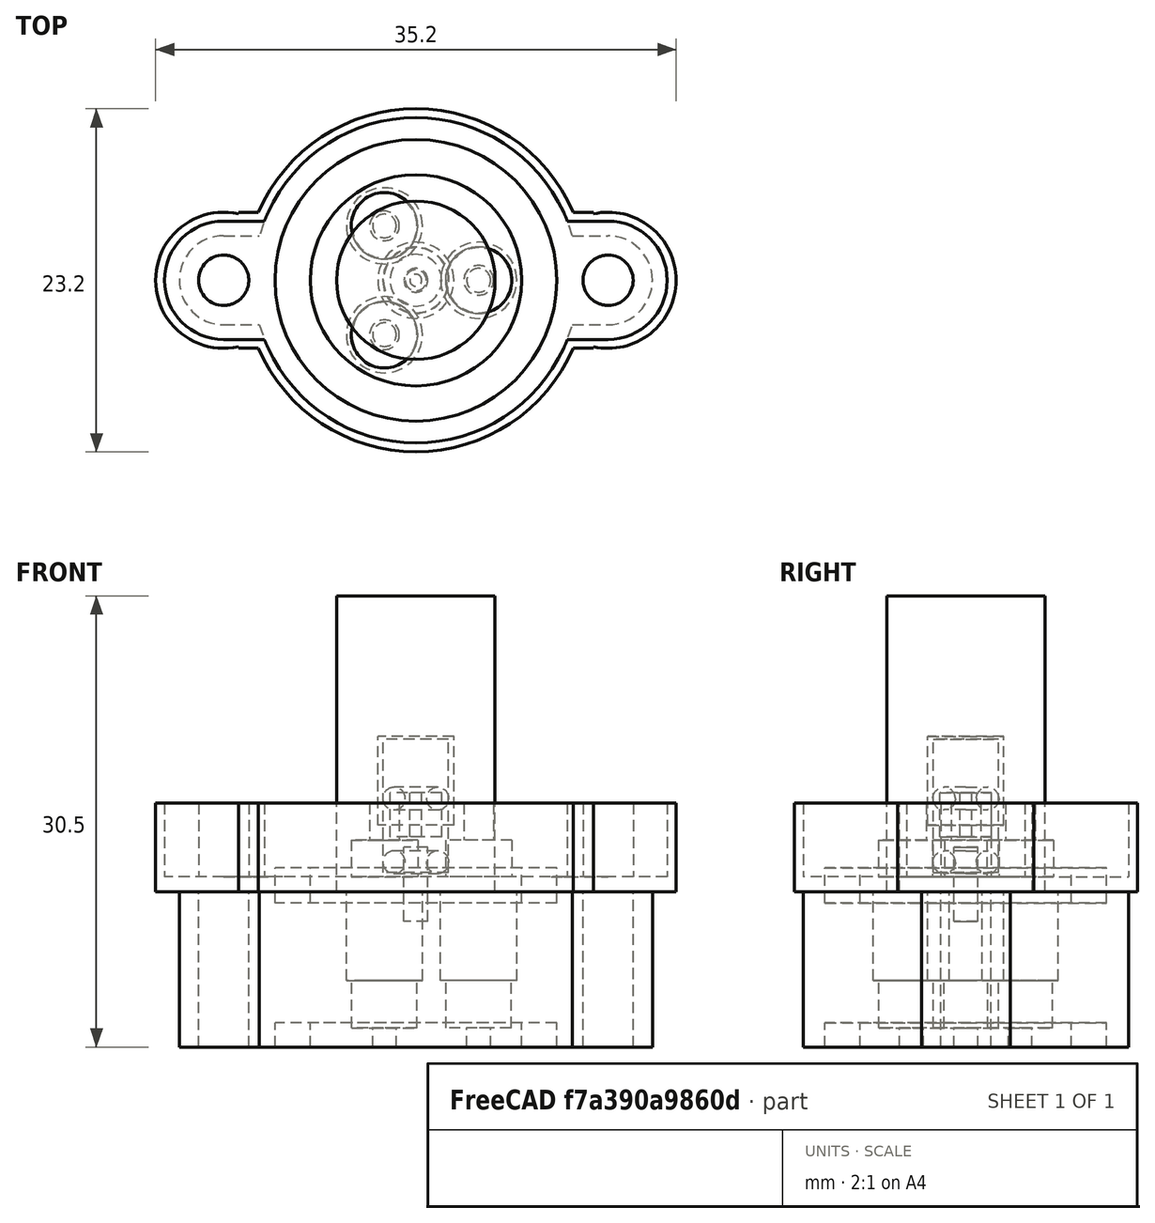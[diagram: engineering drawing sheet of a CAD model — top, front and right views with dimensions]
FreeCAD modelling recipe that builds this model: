
FCSTD DOCUMENT  (FreeCAD 0.17R13509 (Git))
Label: ceramic_wire_feedthroughs_negative
License: All rights reserved
LicenseURL: http://en.wikipedia.org/wiki/All_rights_reserved
objects: Part::Cylinder×49, Part::MultiFuse×13, Part::Cut×10, Part::Box×10, Part::FeaturePython×4, Part::Feature×2, App::FeaturePython×1
note: 88 computed .brp shape members not serialized (recipe doc carries the construction recipe); baked Part::Feature solids carry a one-line shape summary decoded from their .brp

FEATURE [Part::Cylinder] Cylinder151  label="WireFeedsMount002"
  Angle = 360
  AttacherType = Attacher::AttachEngine3D
  Height = 11
  Placement = pos=(13,0,0) rot=(0,0,1;0rad)
  Radius = 1.7
FEATURE [Part::Cylinder] Cylinder155  label="Cylinder009"
  Angle = 360
  AttacherType = Attacher::AttachEngine3D
  Height = 2.38125
  Radius = 9.525
  expr: Radius = 3 / 4 * 25.399999999999999 / 2
  expr: Height = 3 / 32 * 25.399999999999999
FEATURE [Part::Cylinder] Cylinder154  label="Cylinder008"
  Angle = 360
  AttacherType = Attacher::AttachEngine3D
  Height = 2.38125
  Radius = 7.14375
  expr: Radius = 9 / 16 * 25.399999999999999 / 2
  expr: Height = 3 / 32 * 25.399999999999999
FEATURE [Part::Feature] Part__Feature001  label="TopOring"
  Placement = pos=(0,0,6.3) rot=(0,0,1;0rad)
  shape: bbox 4.839 x 4.839 x 1.524 mm, 4 faces (baked)
FEATURE [Part::Feature] Part__Feature002  label="BottomOring"
  Placement = pos=(0,0,2) rot=(0,0,1;0rad)
  shape: bbox 4.839 x 4.839 x 1.524 mm, 4 faces (baked)
FEATURE [Part::Cylinder] Cylinder153  label="Body"
  Angle = 360
  AttacherType = Attacher::AttachEngine3D
  Height = 5
  Radius = 11
FEATURE [Part::Cut] Cut019  label="Oring"
  Base = -> Cylinder155
  Placement = pos=(0,0,-0.75) rot=(0,0,1;0rad)
  Tool = -> Cylinder154
FEATURE [Part::Cylinder] Cylinder150  label="WireFeedsMount1"
  Angle = 360
  AttacherType = Attacher::AttachEngine3D
  Height = 11
  Placement = pos=(-13,0,0) rot=(0,0,1;0rad)
  Radius = 1.7
FEATURE [Part::Cylinder] Cylinder147  label="ThreadedSection"
  Angle = 360
  AttacherType = Attacher::AttachEngine3D
  Height = 1
  Placement = pos=(0,0,4.5) rot=(0,0,1;0rad)
  Radius = 1
FEATURE [Part::Cylinder] Cylinder149  label="FTBead"
  Angle = 360
  AttacherType = Attacher::AttachEngine3D
  Height = 3
  Placement = pos=(0,0,2.7) rot=(0,0,1;0rad)
  Radius = 1.75
  expr: Radius = 3.5 / 2
FEATURE [Part::Cylinder] Cylinder152  label="RFFeeds005"
  Angle = 360
  AttacherType = Attacher::AttachEngine3D
  Height = 20
  Radius = 5.35813
  expr: Placement.Base.x = 0
FEATURE [Part::Cylinder] Cylinder156  label="BottomWireOutlet"
  Angle = 360
  AttacherType = Attacher::AttachEngine3D
  Height = 5
  Placement = pos=(0,0,-2) rot=(0,0,1;0rad)
  Radius = 1
FEATURE [Part::Cylinder] Cylinder157  label="SealSubtraction"
  Angle = 360
  AttacherType = Attacher::AttachEngine3D
  Height = 8
  Placement = pos=(0,0,2.5) rot=(0,0,1;0rad)
  Radius = 2.25
FEATURE [Part::Cylinder] Cylinder  label="MountFlange1"
  Angle = 360
  AttacherType = Attacher::AttachEngine3D
  Height = 5
  Placement = pos=(-13,0,0) rot=(0,0,1;0rad)
  Radius = 4
FEATURE [Part::Box] Box  label="MountCube1"
  AttacherType = Attacher::AttachEngine3D
  Height = 5
  Length = 3
  Placement = pos=(-13,-4,0) rot=(0,0,1;0rad)
  Width = 8
FEATURE [Part::Box] Box001  label="MountCube002"
  AttacherType = Attacher::AttachEngine3D
  Height = 5
  Length = 3
  Placement = pos=(10,-4,0) rot=(0,0,1;0rad)
  Width = 8
FEATURE [Part::Cylinder] Cylinder158  label="MountFlange002"
  Angle = 360
  AttacherType = Attacher::AttachEngine3D
  Height = 5
  Placement = pos=(13,0,0) rot=(0,0,1;0rad)
  Radius = 4
FEATURE [Part::MultiFuse] Fusion
  Placement = pos=(4.25,0,0) rot=(0,0,1;0rad)
  Shapes = -> [Cylinder147,Cylinder157,Cylinder156]
FEATURE [Part::FeaturePython] Array  label="SealArray"  # Draft array (typed FeaturePython)
  Angle = 360
  ArrayType = 1
  Axis = (0,0,1)
  Base = -> Fusion
  Center = (0,0,0)
  Fuse = false
  IntervalAxis = (0,0,0)
  IntervalX = (1,0,0)
  IntervalY = (0,1,0)
  IntervalZ = (0,0,0)
  NumberPolar = 3
  NumberX = 2
  NumberY = 2
  NumberZ = 1
FEATURE [Part::Cylinder] Cylinder159  label="FTBeadHole"
  Angle = 360
  AttacherType = Attacher::AttachEngine3D
  Height = 17
  Radius = 0.405
  expr: Radius = 0.81000000000000005 / 2
FEATURE [Part::Cut] Cut020
  Base = -> Cylinder149
  Placement = pos=(0,0,1) rot=(0,0,1;0rad)
  Tool = -> Cylinder159
FEATURE [Part::Cylinder] Cylinder160  label="Cylinder010"
  Angle = 360
  AttacherType = Attacher::AttachEngine3D
  Height = 2.38125
  Radius = 9.525
  expr: Radius = 3 / 4 * 25.399999999999999 / 2
  expr: Height = 3 / 32 * 25.399999999999999
FEATURE [Part::Cylinder] Cylinder161  label="WireFeedsMount003"
  Angle = 360
  AttacherType = Attacher::AttachEngine3D
  Height = 11
  Placement = pos=(-13,0,0) rot=(0,0,1;0rad)
  Radius = 1.7
FEATURE [Part::Cylinder] Cylinder162  label="ThreadedSection001"
  Angle = 360
  AttacherType = Attacher::AttachEngine3D
  Height = 6
  Placement = pos=(0,0,4.5) rot=(0,0,1;0rad)
  Radius = 2.575
  expr: Radius = 5.1500000000000004 / 2
FEATURE [Part::Cylinder] Cylinder163  label="Cylinder011"
  Angle = 360
  AttacherType = Attacher::AttachEngine3D
  Height = 2.38125
  Radius = 7.14375
  expr: Radius = 9 / 16 * 25.399999999999999 / 2
  expr: Height = 3 / 32 * 25.399999999999999
FEATURE [Part::Cut] Cut022  label="Oring001"
  Base = -> Cylinder160
  Placement = pos=(0,0,-0.75) rot=(0,0,1;0rad)
  Tool = -> Cylinder163
FEATURE [Part::Cylinder] Cylinder164  label="Body001"
  Angle = 360
  AttacherType = Attacher::AttachEngine3D
  Height = 10.5
  Radius = 11
FEATURE [Part::Cylinder] Cylinder165  label="WireFeedsMount004"
  Angle = 360
  AttacherType = Attacher::AttachEngine3D
  Height = 11
  Placement = pos=(13,0,0) rot=(0,0,1;0rad)
  Radius = 1.7
FEATURE [Part::Cylinder] Cylinder166  label="BottomWireOutlet001"
  Angle = 360
  AttacherType = Attacher::AttachEngine3D
  Height = 5
  Placement = pos=(0,0,-2) rot=(0,0,1;0rad)
  Radius = 0.8
FEATURE [Part::Cylinder] Cylinder167  label="SealSubtraction001"
  Angle = 360
  AttacherType = Attacher::AttachEngine3D
  Height = 9
  Placement = pos=(0,0,1.3) rot=(0,0,1;0rad)
  Radius = 2.2
FEATURE [Part::Box] Box002  label="MountCube003"
  AttacherType = Attacher::AttachEngine3D
  Height = 10.5
  Length = 3
  Placement = pos=(10,-3,0) rot=(0,0,1;0rad)
  Width = 6
FEATURE [Part::Box] Box003  label="MountCube004"
  AttacherType = Attacher::AttachEngine3D
  Height = 10.5
  Length = 3
  Placement = pos=(-13,-3,0) rot=(0,0,1;0rad)
  Width = 6
FEATURE [Part::MultiFuse] Fusion004
  Placement = pos=(4.25,0,0) rot=(0,0,1;0rad)
  Shapes = -> [Cylinder162,Cylinder167,Cylinder166]
FEATURE [Part::Cylinder] Cylinder168  label="MountFlange003"
  Angle = 360
  AttacherType = Attacher::AttachEngine3D
  Height = 10.5
  Placement = pos=(-13,0,0) rot=(0,0,1;0rad)
  Radius = 3
FEATURE [Part::Cylinder] Cylinder169  label="MountFlange004"
  Angle = 360
  AttacherType = Attacher::AttachEngine3D
  Height = 10.5
  Placement = pos=(13,0,0) rot=(0,0,1;0rad)
  Radius = 3
FEATURE [Part::MultiFuse] Fusion003
  Shapes = -> [Cylinder169,Box002,Box003,Cylinder168,Cylinder164]
FEATURE [Part::FeaturePython] Array001  label="SealArray001"  # Draft array (typed FeaturePython)
  Angle = 360
  ArrayType = 1
  Axis = (0,0,1)
  Base = -> Fusion004
  Center = (0,0,0)
  Fuse = false
  IntervalAxis = (0,0,0)
  IntervalX = (1,0,0)
  IntervalY = (0,1,0)
  IntervalZ = (0,0,0)
  NumberPolar = 3
  NumberX = 2
  NumberY = 2
  NumberZ = 1
FEATURE [Part::MultiFuse] Fusion005
  Shapes = -> [Cylinder165,Cylinder161,Cut022,Array001]
FEATURE [Part::Cut] Cut021
  Base = -> Fusion003
  Placement = pos=(0,0,-10.5) rot=(0,0,1;0rad)
  Tool = -> Fusion005
FEATURE [Part::Cylinder] Cylinder170  label="Cylinder012"
  Angle = 360
  AttacherType = Attacher::AttachEngine3D
  Height = 2.38125
  Radius = 9.525
  expr: Radius = 3 / 4 * 25.399999999999999 / 2
  expr: Height = 3 / 32 * 25.399999999999999
FEATURE [Part::Cylinder] Cylinder171  label="WireFeedsMount005"
  Angle = 360
  AttacherType = Attacher::AttachEngine3D
  Height = 11
  Placement = pos=(-13,0,0) rot=(0,0,1;0rad)
  Radius = 1.7
FEATURE [Part::Cylinder] Cylinder172  label="ThreadedSection002"
  Angle = 360
  AttacherType = Attacher::AttachEngine3D
  Height = 6
  Placement = pos=(0,0,4.5) rot=(0,0,1;0rad)
  Radius = 2.575
  expr: Radius = 5.1500000000000004 / 2
FEATURE [Part::Cylinder] Cylinder173  label="Cylinder013"
  Angle = 360
  AttacherType = Attacher::AttachEngine3D
  Height = 2.38125
  Radius = 7.14375
  expr: Radius = 9 / 16 * 25.399999999999999 / 2
  expr: Height = 3 / 32 * 25.399999999999999
FEATURE [Part::Cut] Cut024  label="Oring002"
  Base = -> Cylinder170
  Placement = pos=(0,0,-0.75) rot=(0,0,1;0rad)
  Tool = -> Cylinder173
FEATURE [Part::Cylinder] Cylinder174  label="Body002"
  Angle = 360
  AttacherType = Attacher::AttachEngine3D
  Height = 10.5
  Radius = 11
FEATURE [Part::Cylinder] Cylinder175  label="WireFeedsMount006"
  Angle = 360
  AttacherType = Attacher::AttachEngine3D
  Height = 11
  Placement = pos=(13,0,0) rot=(0,0,1;0rad)
  Radius = 1.7
FEATURE [Part::Cylinder] Cylinder176  label="BottomWireOutlet002"
  Angle = 360
  AttacherType = Attacher::AttachEngine3D
  Height = 5
  Placement = pos=(0,0,-2) rot=(0,0,1;0rad)
  Radius = 0.8
FEATURE [Part::Cylinder] Cylinder177  label="SealSubtraction002"
  Angle = 360
  AttacherType = Attacher::AttachEngine3D
  Height = 9
  Placement = pos=(0,0,1.3) rot=(0,0,1;0rad)
  Radius = 2.2
FEATURE [Part::Box] Box004  label="MountCube005"
  AttacherType = Attacher::AttachEngine3D
  Height = 10.5
  Length = 3
  Placement = pos=(10,-3,0) rot=(0,0,1;0rad)
  Width = 6
FEATURE [App::FeaturePython] SetupSheet002  # Path/CAM operation (typed FeaturePython)
  ClearanceHeightExpression = StartDepth+SetupSheet.ClearanceHeightOffset
  ClearanceHeightOffset = 5
  FinalDepthExpression = OpFinalDepth
  HorizRapid = 0
  SafeHeightExpression = StartDepth+SetupSheet.SafeHeightOffset
  SafeHeightOffset = 3
  StartDepthExpression = OpStartDepth
  StepDownExpression = OpToolDiameter
  VertRapid = 0
FEATURE [Part::Box] Box005  label="MountCube006"
  AttacherType = Attacher::AttachEngine3D
  Height = 10.5
  Length = 3
  Placement = pos=(-13,-3,0) rot=(0,0,1;0rad)
  Width = 6
FEATURE [Part::MultiFuse] Fusion007
  Placement = pos=(4.25,0,0) rot=(0,0,1;0rad)
  Shapes = -> [Cylinder172,Cylinder177,Cylinder176]
FEATURE [Part::Cylinder] Cylinder178  label="MountFlange005"
  Angle = 360
  AttacherType = Attacher::AttachEngine3D
  Height = 10.5
  Placement = pos=(-13,0,0) rot=(0,0,1;0rad)
  Radius = 3
FEATURE [Part::Cylinder] Cylinder179  label="MountFlange006"
  Angle = 360
  AttacherType = Attacher::AttachEngine3D
  Height = 10.5
  Placement = pos=(13,0,0) rot=(0,0,1;0rad)
  Radius = 3
FEATURE [Part::MultiFuse] Fusion006
  Shapes = -> [Cylinder179,Box004,Box005,Cylinder178,Cylinder174]
FEATURE [Part::FeaturePython] Array002  label="SealArray002"  # Draft array (typed FeaturePython)
  Angle = 360
  ArrayType = 1
  Axis = (0,0,1)
  Base = -> Fusion007
  Center = (0,0,0)
  Fuse = false
  IntervalAxis = (0,0,0)
  IntervalX = (1,0,0)
  IntervalY = (0,1,0)
  IntervalZ = (0,0,0)
  NumberPolar = 3
  NumberX = 2
  NumberY = 2
  NumberZ = 1
FEATURE [Part::MultiFuse] Fusion008
  Shapes = -> [Cylinder175,Cylinder171,Cut024,Array002]
FEATURE [Part::Cut] Cut023
  Base = -> Fusion006
  Placement = pos=(0,0,-10.5) rot=(0,0,1;0rad)
  Tool = -> Fusion008
FEATURE [Part::Cylinder] Cylinder180  label="Cylinder014"
  Angle = 360
  AttacherType = Attacher::AttachEngine3D
  Height = 2.38125
  Radius = 7.14375
  expr: Radius = 9 / 16 * 25.399999999999999 / 2
  expr: Height = 3 / 32 * 25.399999999999999
FEATURE [Part::Cylinder] Cylinder181  label="MountFlange007"
  Angle = 360
  AttacherType = Attacher::AttachEngine3D
  Height = 10.5
  Placement = pos=(-13,0,0) rot=(0,0,1;0rad)
  Radius = 3
FEATURE [Part::Box] Box006  label="MountCube007"
  AttacherType = Attacher::AttachEngine3D
  Height = 10.5
  Length = 3
  Placement = pos=(-13,-3,0) rot=(0,0,1;0rad)
  Width = 6
FEATURE [Part::Cylinder] Cylinder182  label="WireFeedsMount007"
  Angle = 360
  AttacherType = Attacher::AttachEngine3D
  Height = 11
  Placement = pos=(13,0,0) rot=(0,0,1;0rad)
  Radius = 1.7
FEATURE [Part::Box] Box007  label="MountCube008"
  AttacherType = Attacher::AttachEngine3D
  Height = 10.5
  Length = 3
  Placement = pos=(10,-3,0) rot=(0,0,1;0rad)
  Width = 6
FEATURE [Part::Cylinder] Cylinder183  label="WireFeedsMount008"
  Angle = 360
  AttacherType = Attacher::AttachEngine3D
  Height = 11
  Placement = pos=(-13,0,0) rot=(0,0,1;0rad)
  Radius = 1.7
FEATURE [Part::Cylinder] Cylinder184  label="Body003"
  Angle = 360
  AttacherType = Attacher::AttachEngine3D
  Height = 10.5
  Radius = 11
FEATURE [Part::Cylinder] Cylinder185  label="MountFlange008"
  Angle = 360
  AttacherType = Attacher::AttachEngine3D
  Height = 10.5
  Placement = pos=(13,0,0) rot=(0,0,1;0rad)
  Radius = 3
FEATURE [Part::Cylinder] Cylinder186  label="BottomWireOutlet003"
  Angle = 360
  AttacherType = Attacher::AttachEngine3D
  Height = 5
  Placement = pos=(0,0,-2) rot=(0,0,1;0rad)
  Radius = 0.8
FEATURE [Part::MultiFuse] Fusion011
  Shapes = -> [Cylinder185,Box007,Box006,Cylinder181,Cylinder184]
FEATURE [Part::Cylinder] Cylinder187  label="ThreadedSection003"
  Angle = 360
  AttacherType = Attacher::AttachEngine3D
  Height = 6
  Placement = pos=(0,0,4.5) rot=(0,0,1;0rad)
  Radius = 2.575
  expr: Radius = 5.1500000000000004 / 2
FEATURE [Part::Cylinder] Cylinder188  label="Cylinder015"
  Angle = 360
  AttacherType = Attacher::AttachEngine3D
  Height = 2.38125
  Radius = 9.525
  expr: Radius = 3 / 4 * 25.399999999999999 / 2
  expr: Height = 3 / 32 * 25.399999999999999
FEATURE [Part::Cut] Cut025  label="Oring003"
  Base = -> Cylinder188
  Placement = pos=(0,0,-0.75) rot=(0,0,1;0rad)
  Tool = -> Cylinder180
FEATURE [Part::Cylinder] Cylinder189  label="SealSubtraction003"
  Angle = 360
  AttacherType = Attacher::AttachEngine3D
  Height = 9
  Placement = pos=(0,0,1.3) rot=(0,0,1;0rad)
  Radius = 2.2
FEATURE [Part::MultiFuse] Fusion009
  Placement = pos=(4.25,0,0) rot=(0,0,1;0rad)
  Shapes = -> [Cylinder187,Cylinder189,Cylinder186]
FEATURE [Part::FeaturePython] Array003  label="SealArray003"  # Draft array (typed FeaturePython)
  Angle = 360
  ArrayType = 1
  Axis = (0,0,1)
  Base = -> Fusion009
  Center = (0,0,0)
  Fuse = false
  IntervalAxis = (0,0,0)
  IntervalX = (1,0,0)
  IntervalY = (0,1,0)
  IntervalZ = (0,0,0)
  NumberPolar = 3
  NumberX = 2
  NumberY = 2
  NumberZ = 1
FEATURE [Part::MultiFuse] Fusion010
  Shapes = -> [Cylinder182,Cylinder183,Cut025,Array003]
FEATURE [Part::Cut] Cut026
  Base = -> Fusion011
  Placement = pos=(0,0,-10.5) rot=(0,0,1;0rad)
  Tool = -> Fusion010
FEATURE [Part::Cylinder] Cylinder192  label="ThreadedSection004"
  Angle = 360
  AttacherType = Attacher::AttachEngine3D
  Height = 6
  Placement = pos=(0,0,4.5) rot=(0,0,1;0rad)
  Radius = 2.575
  expr: Radius = 5.1500000000000004 / 2
FEATURE [Part::Cylinder] Cylinder196  label="BottomWireOutlet004"
  Angle = 360
  AttacherType = Attacher::AttachEngine3D
  Height = 5
  Placement = pos=(0,0,-2) rot=(0,0,1;0rad)
  Radius = 0.8
FEATURE [Part::Cylinder] Cylinder197  label="SealSubtraction004"
  Angle = 360
  AttacherType = Attacher::AttachEngine3D
  Height = 9
  Placement = pos=(0,0,1.3) rot=(0,0,1;0rad)
  Radius = 2.2
FEATURE [Part::MultiFuse] Fusion012
  Shapes = -> [Cylinder,Box,Cylinder153,Box001,Cylinder158]
FEATURE [Part::MultiFuse] Fusion013
  Shapes = -> [Array,Cylinder150,Cylinder151]
FEATURE [Part::Cut] Cut
  Base = -> Fusion012
  Placement = pos=(0,0,6) rot=(1,0,0;3.14159rad)
  Tool = -> Fusion013
FEATURE [Part::Cylinder] Cylinder198  label="Cylinder"
  Angle = 360
  AttacherType = Attacher::AttachEngine3D
  Height = 6
  Radius = 11.6
FEATURE [Part::Cylinder] Cylinder199  label="Cylinder016"
  Angle = 360
  AttacherType = Attacher::AttachEngine3D
  Height = 6
  Placement = pos=(-13,0,0) rot=(0,0,1;0rad)
  Radius = 4.6
FEATURE [Part::Cylinder] Cylinder200  label="Cylinder017"
  Angle = 360
  AttacherType = Attacher::AttachEngine3D
  Height = 6
  Placement = pos=(13,0,0) rot=(0,0,1;0rad)
  Radius = 4.6
FEATURE [Part::Box] Box008  label="Cube"
  AttacherType = Attacher::AttachEngine3D
  Height = 6
  Length = 2
  Placement = pos=(-12,-4.6,0) rot=(0,0,1;0rad)
  Width = 9.2
FEATURE [Part::Box] Box009  label="Cube001"
  AttacherType = Attacher::AttachEngine3D
  Height = 6
  Length = 2
  Placement = pos=(10,-4.6,0) rot=(0,0,1;0rad)
  Width = 9.2
FEATURE [Part::MultiFuse] Fusion014
  Shapes = -> [Box009,Box008,Cylinder198,Cylinder199,Cylinder200]
FEATURE [Part::Cut] Cut027
  Base = -> Fusion014
  Tool = -> Cut
